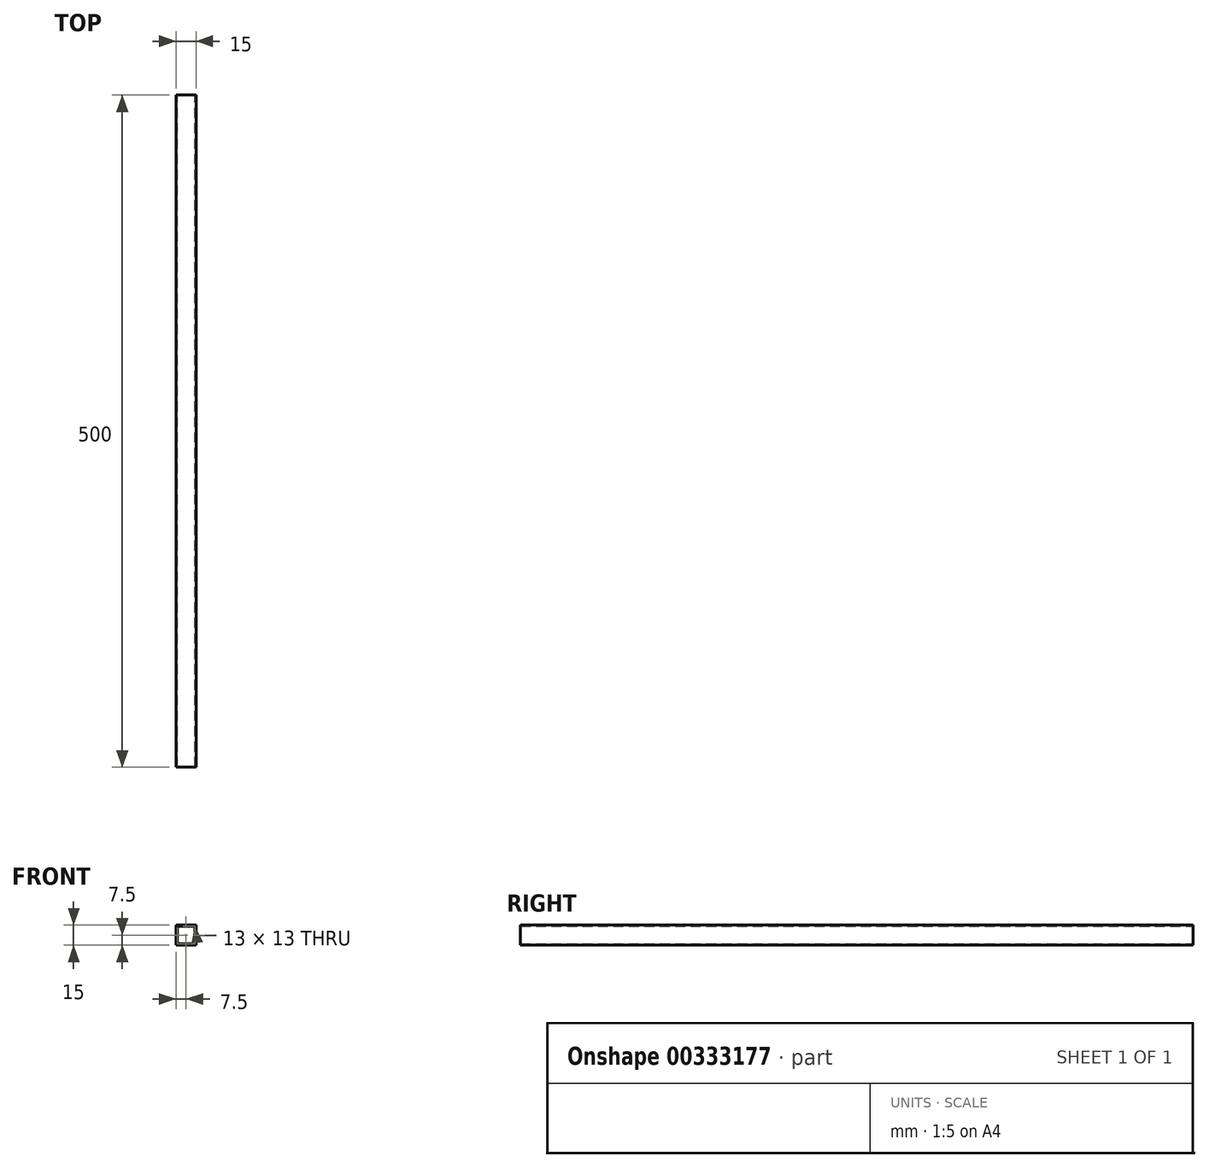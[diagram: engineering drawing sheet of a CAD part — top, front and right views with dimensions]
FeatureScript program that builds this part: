
annotation { "Feature Type Name" : "Feature", "Feature Type Description" : "" }
export const myFeature = defineFeature(function(context is Context, id is Id, definition is map)
    precondition{}
    {
        {
            var Q0;
            Q0=qCreatedBy(makeId("Front.planeOp"),FACE);
            var sketch = newSketch(context, id + "F0", { "sketchPlane" : qUnion([Q0])});
            skLineSegment(sketch, "E0.bottom", {"start": v(7.5, -7.5) * mm, "end": v(-7.5, -7.5) * mm});
            skLineSegment(sketch, "E0.top", {"start": v(7.5, 7.5) * mm, "end": v(-7.5, 7.5) * mm});
            skLineSegment(sketch, "E0.left", {"start": v(7.5, -7.5) * mm, "end": v(7.5, 7.5) * mm});
            skLineSegment(sketch, "E0.right", {"start": v(-7.5, -7.5) * mm, "end": v(-7.5, 7.5) * mm});
            skPoint(sketch, "E0.middle", {"position": v(0, 0) * mm});
            skLineSegment(sketch, "E1.bottom", {"start": v(6.5, -6.5) * mm, "end": v(-6.5, -6.5) * mm});
            skLineSegment(sketch, "E1.top", {"start": v(6.5, 6.5) * mm, "end": v(-6.5, 6.5) * mm});
            skLineSegment(sketch, "E1.left", {"start": v(6.5, -6.5) * mm, "end": v(6.5, 6.5) * mm});
            skLineSegment(sketch, "E1.right", {"start": v(-6.5, -6.5) * mm, "end": v(-6.5, 6.5) * mm});
            skSolve(sketch);
        }
        {
            var Q0;
            Q0=qSketchRegion(id+"F0",true);
            extrude(context, id + "F1", {"entities" : qUnion([Q0]), "endBound" : BoundingType.SYMMETRIC, "depth" : 500 * mm});
        }
    });
